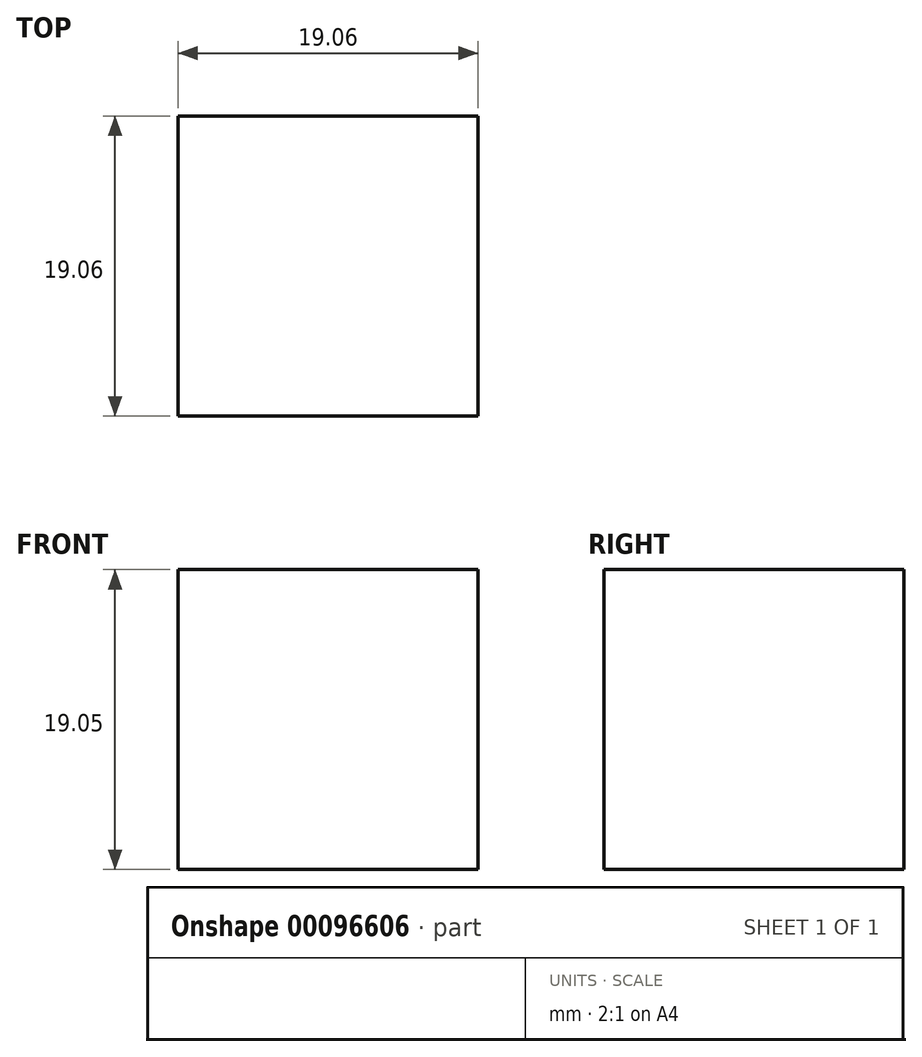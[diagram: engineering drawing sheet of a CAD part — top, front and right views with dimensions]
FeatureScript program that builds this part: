
annotation { "Feature Type Name" : "Feature", "Feature Type Description" : "" }
export const myFeature = defineFeature(function(context is Context, id is Id, definition is map)
    precondition{}
    {
        {
            var Q0;
            Q0=qCreatedBy(makeId("Top.planeOp"),FACE);
            var sketch = newSketch(context, id + "F0", { "sketchPlane" : qUnion([Q0])});
            skLineSegment(sketch, "E0.bottom", {"start": v(9.52, 9.53) * mm, "end": v(-9.53, 9.53) * mm});
            skLineSegment(sketch, "E0.top", {"start": v(9.53, -9.53) * mm, "end": v(-9.52, -9.53) * mm});
            skLineSegment(sketch, "E0.left", {"start": v(9.52, 9.53) * mm, "end": v(9.53, -9.53) * mm});
            skLineSegment(sketch, "E0.right", {"start": v(-9.53, 9.53) * mm, "end": v(-9.52, -9.53) * mm});
            skPoint(sketch, "E0.middle", {"position": v(0, 0) * mm});
            skSolve(sketch);
        }
        {
            var Q0;
            Q0 = qSketchRegion(id + "F0", true);
            extrude(context, id + "F1", {"entities" : qUnion([Q0]), "depth" : 19.05 * mm});
        }
    });
